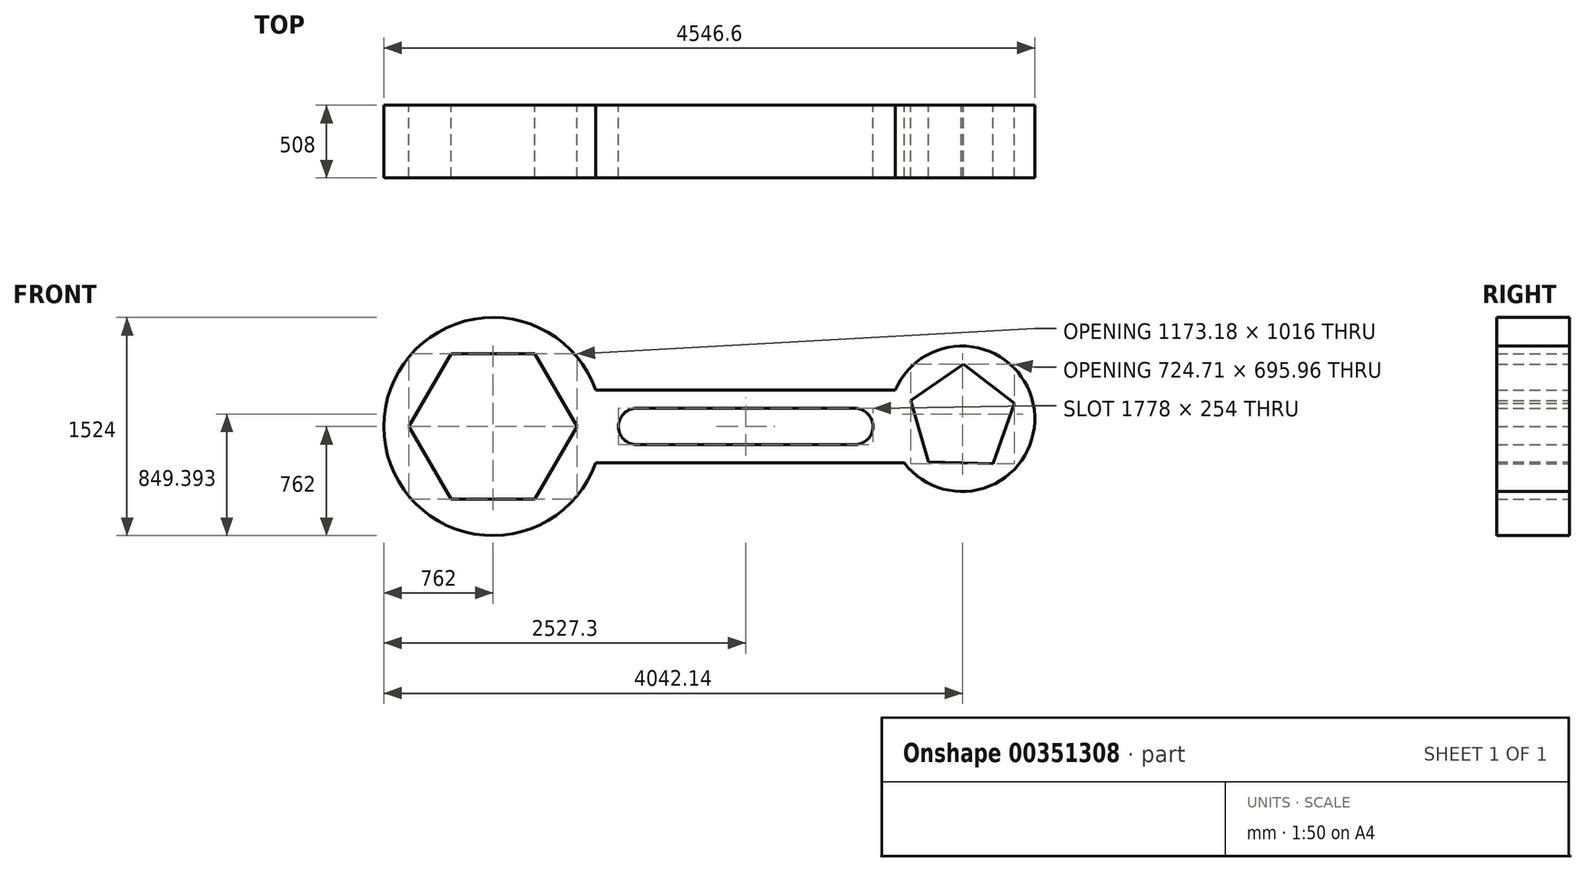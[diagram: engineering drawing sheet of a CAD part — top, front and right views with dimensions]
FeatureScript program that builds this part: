
annotation { "Feature Type Name" : "Feature", "Feature Type Description" : "" }
export const myFeature = defineFeature(function(context is Context, id is Id, definition is map)
    precondition{}
    {
        {
            var Q0;
            Q0=qCreatedBy(makeId("Front.planeOp"),FACE);
            var sketch = newSketch(context, id + "F0", { "sketchPlane" : qUnion([Q0])});
            skCircle(sketch, "E0", {"center": v(0, 0) * mm, "radius": 762 * mm});
            skCircle(sketch, "E1.cCircle", {"center": v(0, 0) * mm, "radius": 508 * mm, "construction": true});
            skLineSegment(sketch, "E1.0", {"start": v(-293.3, 508) * mm, "end": v(293.3, 508) * mm});
            skLineSegment(sketch, "E1.1", {"start": v(293.3, 508) * mm, "end": v(586.59, 0) * mm});
            skLineSegment(sketch, "E1.2", {"start": v(586.59, 0) * mm, "end": v(293.3, -508) * mm});
            skLineSegment(sketch, "E1.3", {"start": v(293.3, -508) * mm, "end": v(-293.3, -508) * mm});
            skLineSegment(sketch, "E1.4", {"start": v(-293.3, -508) * mm, "end": v(-586.59, 0) * mm});
            skLineSegment(sketch, "E1.5", {"start": v(-586.59, 0) * mm, "end": v(-293.3, 508) * mm});
            skPoint(sketch, "E1.0.midPoint", {"position": v(0, 508) * mm});
            skCircle(sketch, "E2.cCircle", {"center": v(3276.6, 54.37) * mm, "radius": 308.37 * mm, "construction": true});
            skLineSegment(sketch, "E2.0", {"start": v(3271.97, -254) * mm, "end": v(3043.4, -247.13) * mm});
            skLineSegment(sketch, "E2.1", {"start": v(3043.4, -247.13) * mm, "end": v(2917.78, 183) * mm});
            skLineSegment(sketch, "E2.2", {"start": v(2917.78, 183) * mm, "end": v(3288.04, 435.37) * mm});
            skLineSegment(sketch, "E2.3", {"start": v(3288.04, 435.37) * mm, "end": v(3642.49, 161.23) * mm});
            skLineSegment(sketch, "E2.4", {"start": v(3642.49, 161.23) * mm, "end": v(3491.29, -260.59) * mm});
            skPoint(sketch, "E2.0.midPoint", {"position": v(3267.34, -253.86) * mm});
            skLineSegment(sketch, "E3", {"start": v(718.42, 254) * mm, "end": v(2809.47, 254) * mm});
            skLineSegment(sketch, "E4", {"start": v(718.42, -254) * mm, "end": v(2872.9, -254) * mm});
            skCircle(sketch, "E5", {"center": v(3276.6, 54.37) * mm, "radius": 508 * mm});
            skPoint(sketch, "E6.orphan", {"position": v(439.94, -254) * mm});
            skLineSegment(sketch, "E7.trimOffspring", {"start": v(2953.97, 59.08) * mm, "end": v(2968.26, 58.87) * mm});
            skPoint(sketch, "E8.trimOffspring.end.orphan", {"position": v(2768.6, 54.37) * mm});
            skPoint(sketch, "E9.trimOffspring.start.orphan", {"position": v(762, 0) * mm});
            skArc(sketch, "E10", {"start": v(2527.3, -127) * mm, "mid": v(2654.3, 0) * mm, "end": v(2527.3, 127) * mm});
            skArc(sketch, "E11", {"start": v(1003.3, 127) * mm, "mid": v(876.3, 0) * mm, "end": v(1003.3, -127) * mm});
            skLineSegment(sketch, "E12", {"start": v(2527.3, -127) * mm, "end": v(1003.3, -127) * mm});
            skLineSegment(sketch, "E13", {"start": v(1003.3, 127) * mm, "end": v(2527.3, 127) * mm});
            skPoint(sketch, "E14.start.orphan", {"position": v(1765.3, 27.19) * mm});
            skPoint(sketch, "E15.end.orphan", {"position": v(876.3, 0) * mm});
            skPoint(sketch, "E16.end.orphan", {"position": v(2654.3, 0) * mm});
            skLineSegment(sketch, "E17", {"start": v(3271.97, -254) * mm, "end": v(3276.6, -254) * mm});
            skLineSegment(sketch, "E18", {"start": v(3276.6, -254) * mm, "end": v(3491.29, -260.59) * mm});
            skSolve(sketch);
        }
        {
            var Q0;
            Q0 = qSketchRegion(id + "F0", true);
            extrude(context, id + "F1", {"entities" : qUnion([Q0]), "depth" : 508 * mm});
        }
    });
